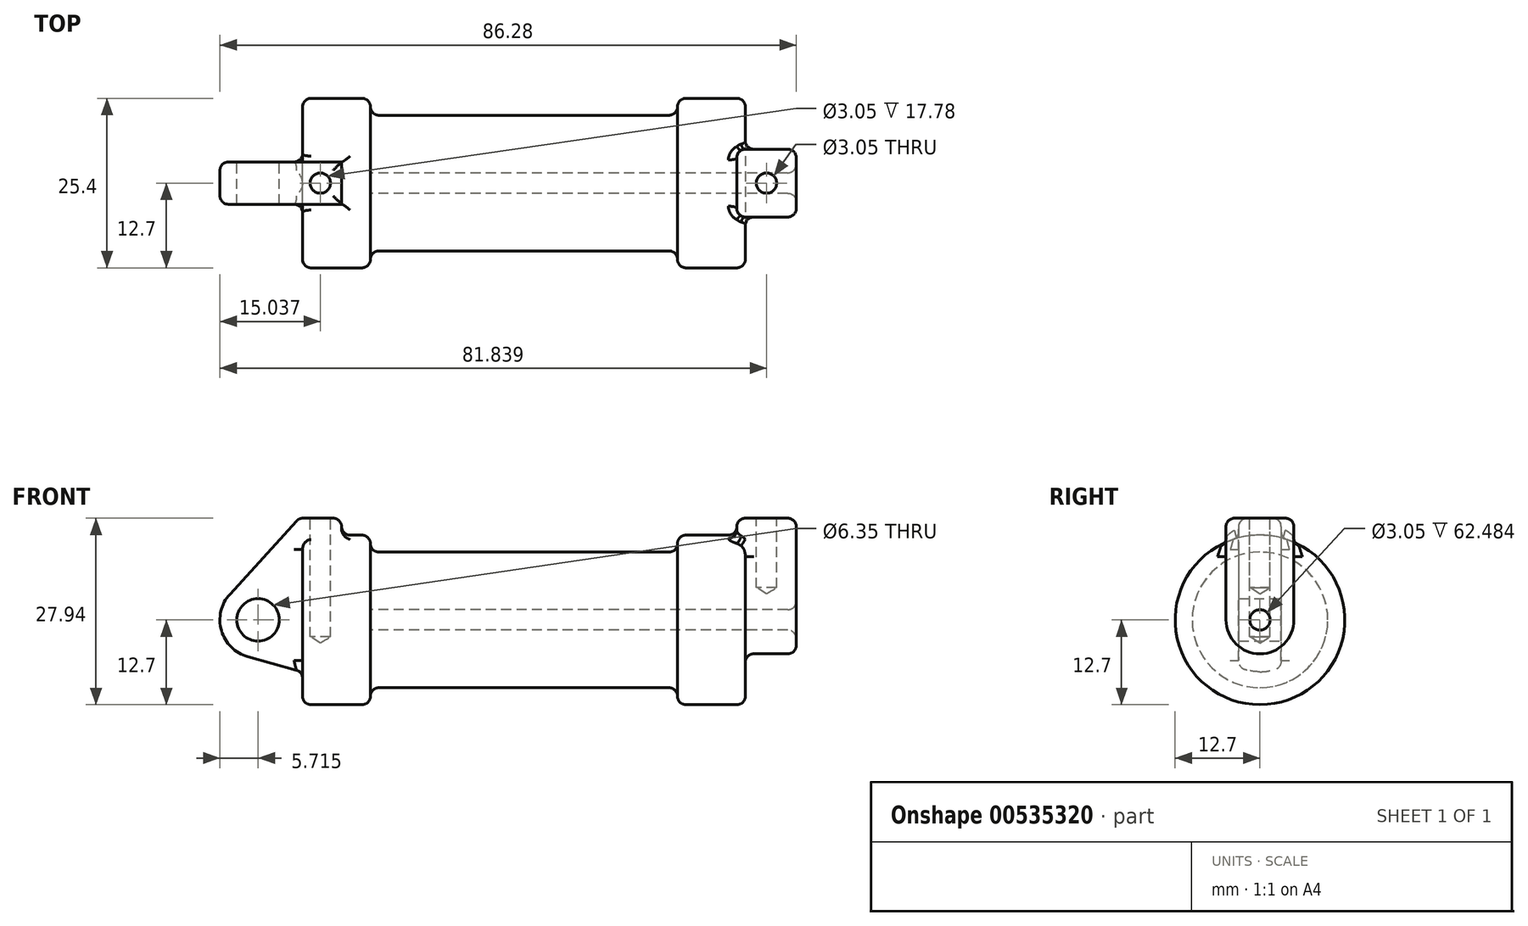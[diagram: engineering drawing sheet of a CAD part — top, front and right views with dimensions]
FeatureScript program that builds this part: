
annotation { "Feature Type Name" : "Feature", "Feature Type Description" : "" }
export const myFeature = defineFeature(function(context is Context, id is Id, definition is map)
    precondition{}
    {
        {
            var Q0;
            Q0=qCreatedBy(makeId("Front.planeOp"),FACE);
            var sketch = newSketch(context, id + "F0", { "sketchPlane" : qUnion([Q0])});
            skLineSegment(sketch, "E0", {"start": v(0, 0) * mm, "end": v(0, 12.7) * mm});
            skLineSegment(sketch, "E1", {"start": v(0, 12.7) * mm, "end": v(10.16, 12.7) * mm});
            skLineSegment(sketch, "E2", {"start": v(10.16, 12.7) * mm, "end": v(10.16, 10.16) * mm});
            skLineSegment(sketch, "E3", {"start": v(10.16, 10.16) * mm, "end": v(56.13, 10.16) * mm});
            skLineSegment(sketch, "E4", {"start": v(56.13, 10.16) * mm, "end": v(56.13, 12.7) * mm});
            skLineSegment(sketch, "E5", {"start": v(56.13, 12.7) * mm, "end": v(66.3, 12.7) * mm});
            skLineSegment(sketch, "E6", {"start": v(66.3, 12.7) * mm, "end": v(66.3, 0) * mm});
            skLineSegment(sketch, "E7", {"start": v(66.3, 0) * mm, "end": v(0, 0) * mm});
            skLineSegment(sketch, "E8", {"start": v(5.84, 15.24) * mm, "end": v(-0.5, 15.24) * mm});
            skLineSegment(sketch, "E9", {"start": v(-0.5, 15.24) * mm, "end": v(-10.88, 3.85) * mm});
            skLineSegment(sketch, "E10", {"start": v(0, 0) * mm, "end": v(-6.65, 0) * mm});
            skCircle(sketch, "E11", {"center": v(-6.65, 0) * mm, "radius": 5.72 * mm});
            skCircle(sketch, "E12", {"center": v(-6.65, 0) * mm, "radius": 3.18 * mm});
            skLineSegment(sketch, "E13", {"start": v(5.84, 15.24) * mm, "end": v(5.84, -9.4) * mm});
            skLineSegment(sketch, "E14", {"start": v(5.84, -9.4) * mm, "end": v(-8.18, -5.5) * mm});
            skSolve(sketch);
        }
        {
            var Q0;
            {var subQ0=sQuery(id+"F0.wireOp",EDGE,"E2");Q0=makeQuery(id+"F0.imprint","IMPRINT",FACE,{"disambiguationData":[TD([[makeQuery(id+"F0.imprint","IMPRINT",EDGE,{"derivedFrom":subQ0}),-1.0]])]});}
            var Q1;
            {var subQ0=sQuery(id+"F0.wireOp",EDGE,"E0");Q1=makeQuery(id+"F0.imprint","IMPRINT",FACE,{"disambiguationData":[TD([[makeQuery(id+"F0.imprint","IMPRINT",EDGE,{"derivedFrom":subQ0}),-1.0]])]});}
            var Q2;
            Q2=sQuery(id+"F0.wireOp",EDGE,"E7");
            revolve(context, id + "F1", {"entities" : qUnion([Q0, Q1]), "axis" : qUnion([Q2]), "revolveType" : RevolveType.FULL});
        }
        {
            var Q0;
            {var subQ0=sQuery(id+"F0.wireOp",EDGE,"E0");Q0=makeQuery(id+"F0.imprint","IMPRINT",FACE,{"disambiguationData":[TD([[makeQuery(id+"F0.imprint","IMPRINT",EDGE,{"derivedFrom":subQ0}),-1.0]])]});}
            var Q1;
            {var subQ1=sQuery(id+"F0.wireOp",EDGE,"E0");Q1=makeQuery(id+"F0.imprint","IMPRINT",FACE,{"disambiguationData":[TD([[makeQuery(id+"F0.imprint","IMPRINT",EDGE,{"derivedFrom":subQ1}),1.0]])]});}
            var Q2;
            {var subQ0=sQuery(id+"F0.wireOp",EDGE,"E14");Q2=makeQuery(id+"F0.imprint","IMPRINT",FACE,{"disambiguationData":[TD([[makeQuery(id+"F0.imprint","IMPRINT",EDGE,{"derivedFrom":subQ0}),-1.0]])]});}
            var Q3;
            {var subQ5=sQuery(id+"F0.wireOp",EDGE,"E12");Q3=makeQuery(id+"F0.imprint","IMPRINT",FACE,{"disambiguationData":[TD([[makeQuery(id+"F0.imprint","IMPRINT",EDGE,{"derivedFrom":subQ5}),-1.0]])]});}
            var Q4;
            Q4=makeQuery(id+"F1.opRevolve","SWEPT_BODY",BODY,{"disambiguationData":[OSD([sQuery(id+"F0.wireOp",EDGE,"E0"),sQuery(id+"F0.wireOp",EDGE,"E1"),sQuery(id+"F0.wireOp",EDGE,"E2"),sQuery(id+"F0.wireOp",EDGE,"E3"),sQuery(id+"F0.wireOp",EDGE,"E4"),sQuery(id+"F0.wireOp",EDGE,"E5"),sQuery(id+"F0.wireOp",EDGE,"E6"),sQuery(id+"F0.wireOp",EDGE,"E7")])]});
            extrude(context, id + "F2", {"entities" : qUnion([Q0, Q1, Q2, Q3]), "operationType" : NewBodyOperationType.ADD, "endBound" : BoundingType.SYMMETRIC, "depth" : 6.35 * mm, "endBoundEntityBody" : qUnion([Q4]), "offsetDistance" : 25.4 * mm});
        }
        {
            var Q0;
            Q0=makeQuery(id+"F1.opRevolve","SWEPT_FACE",FACE,{"disambiguationData":[OSD([sQuery(id+"F0.wireOp",EDGE,"E6")])]});
            var sketch = newSketch(context, id + "F3", { "sketchPlane" : qUnion([Q0])});
            skCircle(sketch, "E15", {"center": v(0, 0) * mm, "radius": 1.52 * mm});
            skCircle(sketch, "E16", {"center": v(0, 0) * mm, "radius": 5.08 * mm});
            skLineSegment(sketch, "E17", {"start": v(-5.08, 0) * mm, "end": v(-5.08, 15.24) * mm});
            skLineSegment(sketch, "E18", {"start": v(-5.08, 15.24) * mm, "end": v(5.08, 15.24) * mm});
            skLineSegment(sketch, "E19", {"start": v(5.08, 15.24) * mm, "end": v(5.08, 0) * mm});
            skSolve(sketch);
        }
        {
            var Q0;
            Q0 = qSketchRegion(id + "F3", true);
            extrude(context, id + "F4", {"entities" : qUnion([Q0]), "operationType" : NewBodyOperationType.ADD, "depth" : 7.62 * mm, "offsetDistance" : 25.4 * mm, "hasSecondDirection" : true, "secondDirectionOppositeDirection" : true, "secondDirectionDepth" : 1.27 * mm});
        }
        {
            var Q0;
            Q0=makeQuery(id+"F3.imprint","IMPRINT",FACE,{"disambiguationData":[TD([[makeQuery(id+"F3.imprint","IMPRINT",EDGE,{"derivedFrom":sQuery(id+"F3.wireOp",EDGE,"E15")}),1.0]])]});
            var Q1;
            Q1=makeQuery(id+"F1.opRevolve","SWEPT_FACE",FACE,{"disambiguationData":[OSD([sQuery(id+"F0.wireOp",EDGE,"E2")])]});
            extrude(context, id + "F5", {"entities" : qUnion([Q0]), "operationType" : NewBodyOperationType.REMOVE, "endBound" : BoundingType.UP_TO_SURFACE, "oppositeDirection" : true, "depth" : 22.86 * mm, "endBoundEntityFace" : qUnion([Q1]), "offsetDistance" : 25.4 * mm});
        }
        {
            var Q0;
            Q0=makeQuery(id+"F2.opExtrude","SWEPT_FACE",FACE,{"disambiguationData":[OSD([sQuery(id+"F0.wireOp",EDGE,"E8")])]});
            var sketch = newSketch(context, id + "F6", { "sketchPlane" : qUnion([Q0])});
            skCircle(sketch, "E20", {"center": v(2.67, 0) * mm, "radius": 1.52 * mm});
            skLineSegment(sketch, "E21", {"start": v(2.67, 3.17) * mm, "end": v(2.67, 0) * mm, "construction": true});
            skLineSegment(sketch, "E22", {"start": v(-0.5, 0) * mm, "end": v(2.67, 0) * mm, "construction": true});
            skSolve(sketch);
        }
        {
            var Q0;
            Q0=sQuery(id+"F6.wireOp",VERTEX,"E21.end");
            var Q1;
            Q1=makeQuery(id+"F1.opRevolve","SWEPT_BODY",BODY,{"disambiguationData":[OSD([sQuery(id+"F0.wireOp",EDGE,"E0"),sQuery(id+"F0.wireOp",EDGE,"E1"),sQuery(id+"F0.wireOp",EDGE,"E2"),sQuery(id+"F0.wireOp",EDGE,"E3"),sQuery(id+"F0.wireOp",EDGE,"E4"),sQuery(id+"F0.wireOp",EDGE,"E5"),sQuery(id+"F0.wireOp",EDGE,"E6"),sQuery(id+"F0.wireOp",EDGE,"E7")])]});
            var Q2;
            Q2=makeQuery(id+"F2.opExtrude","SWEPT_BODY",BODY,{"disambiguationData":[OSD([sQuery(id+"F0.wireOp",EDGE,"E8"),sQuery(id+"F0.wireOp",EDGE,"E9"),sQuery(id+"F0.wireOp",EDGE,"E11"),sQuery(id+"F0.wireOp",EDGE,"E12"),sQuery(id+"F0.wireOp",EDGE,"E13"),sQuery(id+"F0.wireOp",EDGE,"E14")])]});
            hole(context, id + "F7", {"style" : HoleStyle.SIMPLE, "endStyle" : HoleEndStyle.BLIND, "holeDiameter" : 3.05 * mm, "holeDepth" : 17.78 * mm, "isTappedThrough" : true, "tappedDepth" : 12.7 * mm, "tapClearance" : 3, "startFromSketch" : true, "locations" : qUnion([Q0]), "scope" : qUnion([Q1, Q2])});
        }
        {
            var Q0;
            Q0=makeQuery(id+"F4.opExtrude","SWEPT_FACE",FACE,{"disambiguationData":[OSD([sQuery(id+"F3.wireOp",EDGE,"E18")])]});
            var sketch = newSketch(context, id + "F8", { "sketchPlane" : qUnion([Q0])});
            skCircle(sketch, "E23", {"center": v(69.47, 0) * mm, "radius": 1.52 * mm});
            skLineSegment(sketch, "E24", {"start": v(69.47, 5.08) * mm, "end": v(69.47, 0) * mm, "construction": true});
            skLineSegment(sketch, "E25", {"start": v(73.91, 0) * mm, "end": v(69.47, 0) * mm, "construction": true});
            skSolve(sketch);
        }
        {
            var Q0;
            Q0=sQuery(id+"F8.wireOp",VERTEX,"E24.end");
            var Q1;
            Q1=makeQuery(id+"F1.opRevolve","SWEPT_BODY",BODY,{"disambiguationData":[OSD([sQuery(id+"F0.wireOp",EDGE,"E0"),sQuery(id+"F0.wireOp",EDGE,"E1"),sQuery(id+"F0.wireOp",EDGE,"E2"),sQuery(id+"F0.wireOp",EDGE,"E3"),sQuery(id+"F0.wireOp",EDGE,"E4"),sQuery(id+"F0.wireOp",EDGE,"E5"),sQuery(id+"F0.wireOp",EDGE,"E6"),sQuery(id+"F0.wireOp",EDGE,"E7")])]});
            hole(context, id + "F9", {"style" : HoleStyle.SIMPLE, "endStyle" : HoleEndStyle.BLIND, "holeDiameter" : 3.05 * mm, "holeDepth" : 10.4 * mm, "isTappedThrough" : true, "tappedDepth" : 12.7 * mm, "tapClearance" : 3, "startFromSketch" : true, "locations" : qUnion([Q0]), "scope" : qUnion([Q1])});
        }
        {
            var Q0;
            Q0=makeQuery(id+"F1.opRevolve","SWEPT_EDGE",EDGE,{"disambiguationData":[OSD([sQuery(id+"F0.wireOp",EDGE,"E2"),sQuery(id+"F0.wireOp",EDGE,"E3")])]});
            var Q1;
            Q1=makeQuery(id+"F1.opRevolve","SWEPT_EDGE",EDGE,{"disambiguationData":[OSD([sQuery(id+"F0.wireOp",EDGE,"E3"),sQuery(id+"F0.wireOp",EDGE,"E4")])]});
            var Q2;
            Q2=makeQuery(id+"F1.opRevolve","SWEPT_EDGE",EDGE,{"disambiguationData":[OSD([sQuery(id+"F0.wireOp",EDGE,"E1"),sQuery(id+"F0.wireOp",EDGE,"E2")])]});
            var Q3;
            Q3=makeQuery(id+"F1.opRevolve","SWEPT_EDGE",EDGE,{"disambiguationData":[OSD([sQuery(id+"F0.wireOp",EDGE,"E4"),sQuery(id+"F0.wireOp",EDGE,"E5")])]});
            var Q4;
            Q4=makeQuery(id+"F1.opRevolve","SWEPT_EDGE",EDGE,{"disambiguationData":[OSD([sQuery(id+"F0.wireOp",EDGE,"E5"),sQuery(id+"F0.wireOp",EDGE,"E6")])]});
            var Q5;
            Q5=makeQuery(id+"F1.opRevolve","SWEPT_EDGE",EDGE,{"disambiguationData":[OSD([sQuery(id+"F0.wireOp",EDGE,"E0"),sQuery(id+"F0.wireOp",EDGE,"E1")])]});
            fillet(context, id + "F10", {"entities" : qUnion([Q0, Q1, Q2, Q3, Q4, Q5]), "radius" : 1.27 * mm, "tangentPropagation" : true, "allowEdgeOverflow" : false});
        }
        {
            var Q0;
            Q0=makeQuery(id+"F2.boolean.opBoolean","INTERSECT",EDGE,{"derivedFrom":[makeQuery(id+"F1.opRevolve","SWEPT_FACE",FACE,{"disambiguationData":[OSD([sQuery(id+"F0.wireOp",EDGE,"E1")])]}),makeQuery(id+"F2.opExtrude","CAP_FACE",FACE,{"disambiguationData":[OSD([sQuery(id+"F0.wireOp",EDGE,"E8"),sQuery(id+"F0.wireOp",EDGE,"E9"),sQuery(id+"F0.wireOp",EDGE,"E11"),sQuery(id+"F0.wireOp",EDGE,"E12"),sQuery(id+"F0.wireOp",EDGE,"E13"),sQuery(id+"F0.wireOp",EDGE,"E14")])],"isStart":false})]});
            var Q1;
            Q1=makeQuery(id+"F2.boolean.opBoolean","INTERSECT",EDGE,{"derivedFrom":[makeQuery(id+"F1.opRevolve","SWEPT_FACE",FACE,{"disambiguationData":[OSD([sQuery(id+"F0.wireOp",EDGE,"E1")])]}),makeQuery(id+"F2.opExtrude","SWEPT_FACE",FACE,{"disambiguationData":[OSD([sQuery(id+"F0.wireOp",EDGE,"E13")])]})]});
            var Q2;
            Q2=makeQuery(id+"F2.boolean.opBoolean","INTERSECT",EDGE,{"derivedFrom":[makeQuery(id+"F1.opRevolve","SWEPT_FACE",FACE,{"disambiguationData":[OSD([sQuery(id+"F0.wireOp",EDGE,"E1")])]}),makeQuery(id+"F2.opExtrude","CAP_FACE",FACE,{"disambiguationData":[OSD([sQuery(id+"F0.wireOp",EDGE,"E8"),sQuery(id+"F0.wireOp",EDGE,"E9"),sQuery(id+"F0.wireOp",EDGE,"E11"),sQuery(id+"F0.wireOp",EDGE,"E12"),sQuery(id+"F0.wireOp",EDGE,"E13"),sQuery(id+"F0.wireOp",EDGE,"E14")])],"isStart":true})]});
            var Q3;
            Q3=makeQuery(id+"F2.opExtrude","CAP_EDGE",EDGE,{"disambiguationData":[OSD([sQuery(id+"F0.wireOp",EDGE,"E8")])],"isStart":true});
            var Q4;
            Q4=makeQuery(id+"F2.opExtrude","SWEPT_EDGE",EDGE,{"disambiguationData":[OSD([sQuery(id+"F0.wireOp",EDGE,"E8"),sQuery(id+"F0.wireOp",EDGE,"E13")])]});
            var Q5;
            Q5=makeQuery(id+"F2.opExtrude","CAP_EDGE",EDGE,{"disambiguationData":[OSD([sQuery(id+"F0.wireOp",EDGE,"E8")])],"isStart":false});
            var Q6;
            Q6=makeQuery(id+"F2.opExtrude","SWEPT_EDGE",EDGE,{"disambiguationData":[OSD([sQuery(id+"F0.wireOp",EDGE,"E8"),sQuery(id+"F0.wireOp",EDGE,"E9")])]});
            var Q7;
            Q7=makeQuery(id+"F2.opExtrude","SWEPT_FACE",FACE,{"disambiguationData":[OSD([sQuery(id+"F0.wireOp",EDGE,"E9")])]});
            fillet(context, id + "F11", {"entities" : qUnion([Q0, Q1, Q2, Q3, Q4, Q5, Q6, Q7]), "radius" : 1.27 * mm, "tangentPropagation" : true, "allowEdgeOverflow" : false});
        }
        {
            var Q0;
            Q0=makeQuery(id+"F4.opExtrude","CAP_FACE",FACE,{"disambiguationData":[OSD([sQuery(id+"F3.wireOp",EDGE,"E15"),sQuery(id+"F3.wireOp",EDGE,"E16"),sQuery(id+"F3.wireOp",EDGE,"E17"),sQuery(id+"F3.wireOp",EDGE,"E18"),sQuery(id+"F3.wireOp",EDGE,"E19")])],"isStart":true});
            var Q1;
            Q1=makeQuery(id+"F4.opExtrude","SWEPT_FACE",FACE,{"disambiguationData":[OSD([sQuery(id+"F3.wireOp",EDGE,"E17")])]});
            var Q2;
            Q2=makeQuery(id+"F4.opExtrude","CAP_FACE",FACE,{"disambiguationData":[OSD([sQuery(id+"F3.wireOp",EDGE,"E15"),sQuery(id+"F3.wireOp",EDGE,"E16"),sQuery(id+"F3.wireOp",EDGE,"E17"),sQuery(id+"F3.wireOp",EDGE,"E18"),sQuery(id+"F3.wireOp",EDGE,"E19")])],"isStart":false});
            var Q3;
            Q3=makeQuery(id+"F4.opExtrude","SWEPT_FACE",FACE,{"disambiguationData":[OSD([sQuery(id+"F3.wireOp",EDGE,"E19")])]});
            fillet(context, id + "F12", {"entities" : qUnion([Q0, Q1, Q2, Q3]), "radius" : 1.27 * mm, "tangentPropagation" : true, "allowEdgeOverflow" : false});
        }
    });
